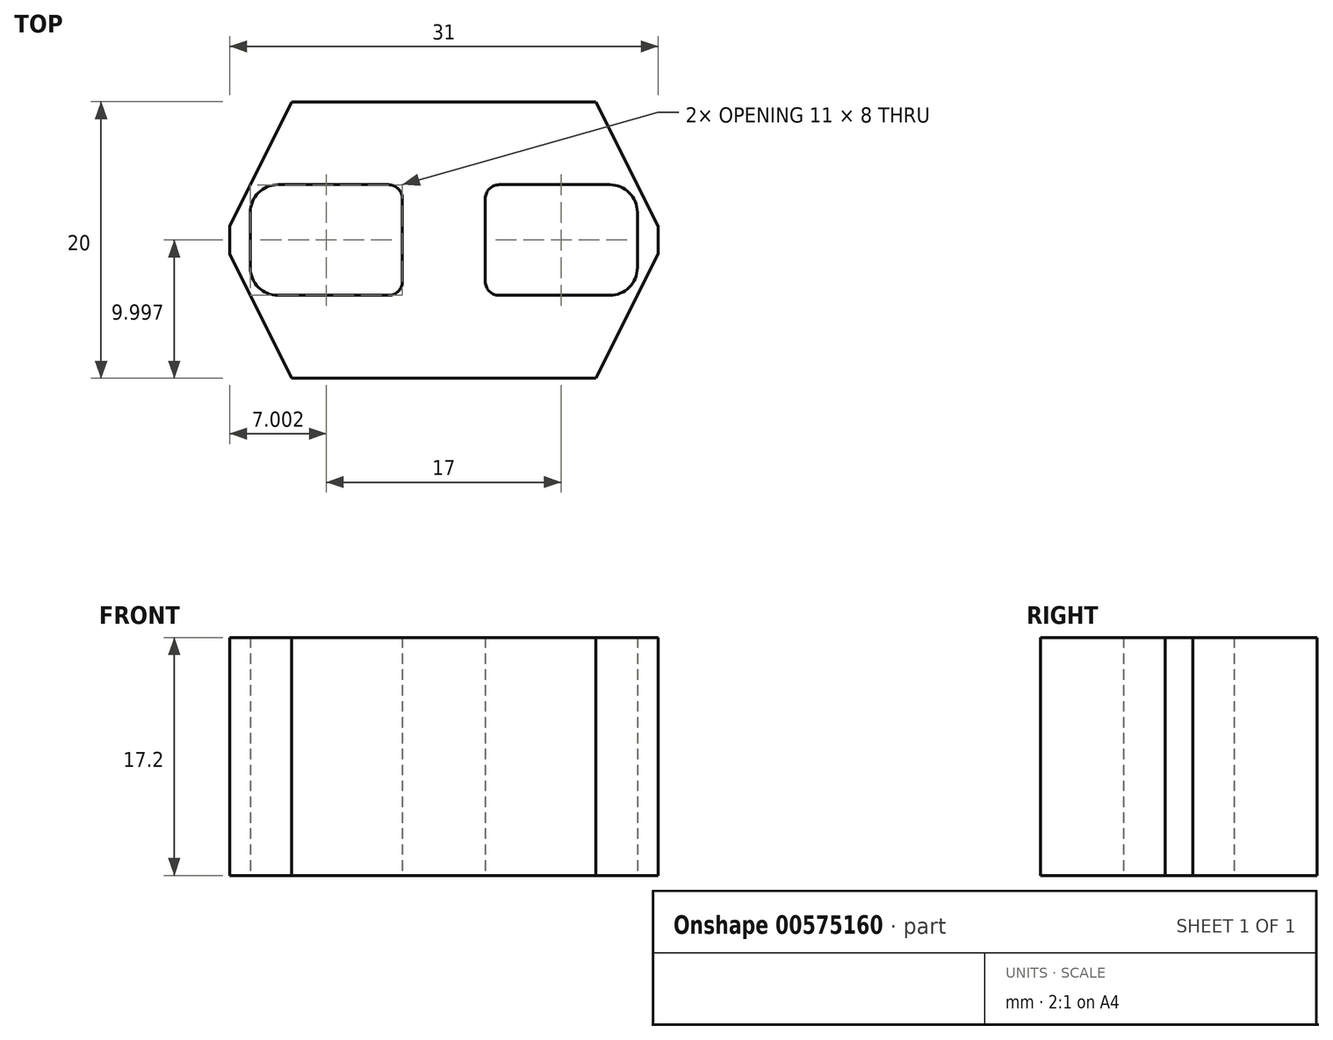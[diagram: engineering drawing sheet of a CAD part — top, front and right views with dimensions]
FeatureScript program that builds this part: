
annotation { "Feature Type Name" : "Feature", "Feature Type Description" : "" }
export const myFeature = defineFeature(function(context is Context, id is Id, definition is map)
    precondition{}
    {
        {
            var Q0;
            Q0=qCreatedBy(makeId("Top.planeOp"),FACE);
            var sketch = newSketch(context, id + "F0", { "sketchPlane" : qUnion([Q0])});
            skLineSegment(sketch, "E0", {"start": v(-63.07, 10.33) * mm, "end": v(-32.07, 10.33) * mm, "construction": true});
            skLineSegment(sketch, "E1", {"start": v(-47.57, 0.33) * mm, "end": v(-47.57, 20.33) * mm, "construction": true});
            skPoint(sketch, "E2", {"position": v(-47.57, 10.33) * mm});
            skLineSegment(sketch, "E3", {"start": v(-63.07, 9.33) * mm, "end": v(-63.07, 11.33) * mm});
            skLineSegment(sketch, "E4", {"start": v(-32.07, 9.33) * mm, "end": v(-32.07, 11.33) * mm});
            skPoint(sketch, "E5", {"position": v(-63.07, 10.33) * mm});
            skPoint(sketch, "E6", {"position": v(-32.07, 10.33) * mm});
            skLineSegment(sketch, "E7", {"start": v(-58.57, 20.33) * mm, "end": v(-36.57, 20.33) * mm});
            skLineSegment(sketch, "E8", {"start": v(-58.57, 0.33) * mm, "end": v(-36.57, 0.33) * mm});
            skPoint(sketch, "E9", {"position": v(-47.57, 20.33) * mm});
            skPoint(sketch, "E10", {"position": v(-47.57, 0.33) * mm});
            skLineSegment(sketch, "E11", {"start": v(-58.57, 20.33) * mm, "end": v(-63.07, 11.33) * mm});
            skLineSegment(sketch, "E12", {"start": v(-63.07, 9.33) * mm, "end": v(-58.57, 0.33) * mm});
            skLineSegment(sketch, "E13", {"start": v(-36.57, 0.33) * mm, "end": v(-32.07, 9.33) * mm});
            skLineSegment(sketch, "E14", {"start": v(-32.07, 11.33) * mm, "end": v(-36.57, 20.33) * mm});
            skLineSegment(sketch, "E15.bottom", {"start": v(-51.57, 14.33) * mm, "end": v(-59.57, 14.33) * mm});
            skLineSegment(sketch, "E15.top", {"start": v(-51.57, 6.33) * mm, "end": v(-59.57, 6.33) * mm});
            skLineSegment(sketch, "E15.left", {"start": v(-50.57, 13.33) * mm, "end": v(-50.57, 7.33) * mm});
            skLineSegment(sketch, "E15.right", {"start": v(-61.57, 12.33) * mm, "end": v(-61.57, 8.33) * mm});
            skPoint(sketch, "E15.middle", {"position": v(-56.07, 10.33) * mm});
            skLineSegment(sketch, "E16.MirrorCS", {"start": v(-33.57, 12.33) * mm, "end": v(-33.57, 8.33) * mm});
            skLineSegment(sketch, "E17.MirrorCS", {"start": v(-44.57, 13.33) * mm, "end": v(-44.57, 7.33) * mm});
            skLineSegment(sketch, "E18.MirrorCS", {"start": v(-43.57, 6.33) * mm, "end": v(-35.57, 6.33) * mm});
            skLineSegment(sketch, "E19.MirrorCS", {"start": v(-43.57, 14.33) * mm, "end": v(-35.57, 14.33) * mm});
            skPoint(sketch, "E20.visualSharp", {"position": v(-61.57, 14.33) * mm});
            skArc(sketch, "E20.filletArc", {"start": v(-59.57, 14.33) * mm, "mid": v(-60.98, 13.74) * mm, "end": v(-61.57, 12.33) * mm});
            skPoint(sketch, "E21.visualSharp", {"position": v(-61.57, 6.33) * mm});
            skArc(sketch, "E21.filletArc", {"start": v(-61.57, 8.33) * mm, "mid": v(-60.98, 6.91) * mm, "end": v(-59.57, 6.33) * mm});
            skPoint(sketch, "E22.visualSharp", {"position": v(-33.57, 6.33) * mm});
            skArc(sketch, "E22.filletArc", {"start": v(-35.57, 6.33) * mm, "mid": v(-34.15, 6.91) * mm, "end": v(-33.57, 8.33) * mm});
            skPoint(sketch, "E23.visualSharp", {"position": v(-33.57, 14.33) * mm});
            skArc(sketch, "E23.filletArc", {"start": v(-33.57, 12.33) * mm, "mid": v(-34.15, 13.74) * mm, "end": v(-35.57, 14.33) * mm});
            skPoint(sketch, "E24.visualSharp", {"position": v(-44.57, 14.33) * mm});
            skArc(sketch, "E24.filletArc", {"start": v(-43.57, 14.33) * mm, "mid": v(-44.27, 14.03) * mm, "end": v(-44.57, 13.33) * mm});
            skPoint(sketch, "E25.visualSharp", {"position": v(-44.57, 6.33) * mm});
            skArc(sketch, "E25.filletArc", {"start": v(-44.57, 7.33) * mm, "mid": v(-44.27, 6.62) * mm, "end": v(-43.57, 6.33) * mm});
            skPoint(sketch, "E26.visualSharp", {"position": v(-50.57, 6.33) * mm});
            skArc(sketch, "E26.filletArc", {"start": v(-51.57, 6.33) * mm, "mid": v(-50.86, 6.62) * mm, "end": v(-50.57, 7.33) * mm});
            skPoint(sketch, "E27.visualSharp", {"position": v(-50.57, 14.33) * mm});
            skArc(sketch, "E27.filletArc", {"start": v(-50.57, 13.33) * mm, "mid": v(-50.86, 14.03) * mm, "end": v(-51.57, 14.33) * mm});
            skSolve(sketch);
        }
        {
            var Q0;
            Q0 = qSketchRegion(id + "F0", true);
            extrude(context, id + "F1", {"entities" : qUnion([Q0]), "depth" : 17.2 * mm, "offsetDistance" : 25 * mm});
        }
    });
